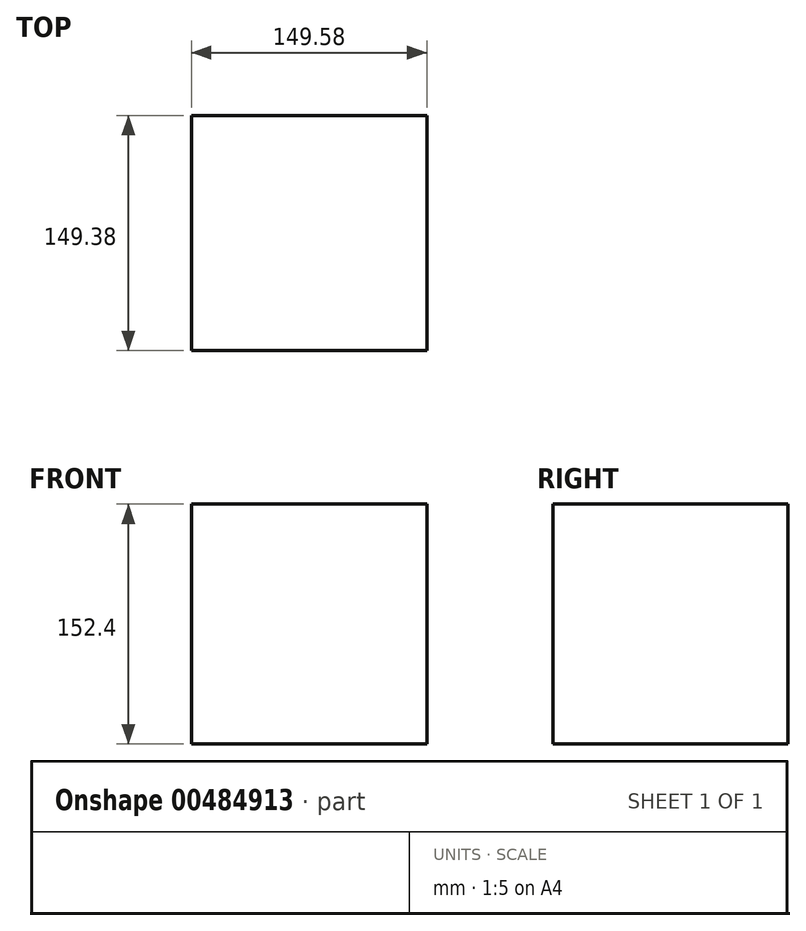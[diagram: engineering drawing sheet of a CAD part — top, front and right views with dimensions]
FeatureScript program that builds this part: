
annotation { "Feature Type Name" : "Feature", "Feature Type Description" : "" }
export const myFeature = defineFeature(function(context is Context, id is Id, definition is map)
    precondition{}
    {
        {
            var Q0;
            Q0=qCreatedBy(makeId("Top.planeOp"),FACE);
            var sketch = newSketch(context, id + "F0", { "sketchPlane" : qUnion([Q0])});
            skLineSegment(sketch, "E0.bottom", {"start": v(-73.95, 74.07) * mm, "end": v(75.63, 74.07) * mm});
            skLineSegment(sketch, "E0.top", {"start": v(-73.95, -75.31) * mm, "end": v(75.63, -75.31) * mm});
            skLineSegment(sketch, "E0.left", {"start": v(-73.95, 74.07) * mm, "end": v(-73.95, -75.31) * mm});
            skLineSegment(sketch, "E0.right", {"start": v(75.63, 74.07) * mm, "end": v(75.63, -75.31) * mm});
            skSolve(sketch);
        }
        {
            var Q0;
            Q0 = qBodyType(qCreatedBy(id + "F0" ,EDGE), BodyType.WIRE);
            var Q1;
            Q1=sQuery(id+"F0.wireOp",EDGE,"E0.bottom");
            extrude(context, id + "F1", {"bodyType" : ToolBodyType.SURFACE, "surfaceEntities" : qUnion([Q0, Q1]), "depth" : 152.4 * mm});
        }
    });
